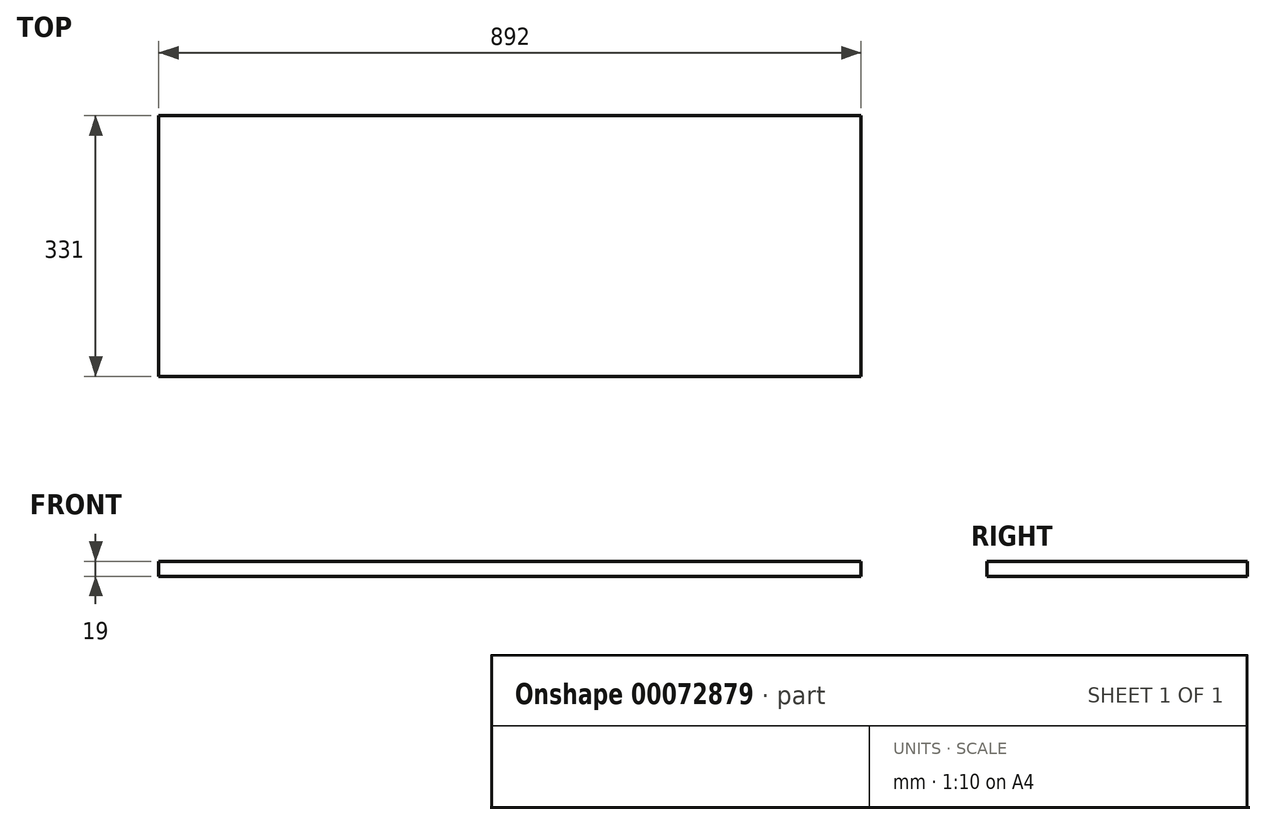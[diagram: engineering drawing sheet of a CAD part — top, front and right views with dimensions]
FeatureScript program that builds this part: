
annotation { "Feature Type Name" : "Feature", "Feature Type Description" : "" }
export const myFeature = defineFeature(function(context is Context, id is Id, definition is map)
    precondition{}
    {
        {
            var Q0;
            Q0=qCreatedBy(makeId("Top.planeOp"),FACE);
            var sketch = newSketch(context, id + "F0", { "sketchPlane" : qUnion([Q0])});
            skLineSegment(sketch, "E0.bottom", {"start": v(0, 0) * mm, "end": v(892, 0) * mm});
            skLineSegment(sketch, "E0.top", {"start": v(0, -331) * mm, "end": v(892, -331) * mm});
            skLineSegment(sketch, "E0.left", {"start": v(0, 0) * mm, "end": v(0, -331) * mm});
            skLineSegment(sketch, "E0.right", {"start": v(892, 0) * mm, "end": v(892, -331) * mm});
            skSolve(sketch);
        }
        {
            var Q0;
            Q0=qSketchRegion(id+"F0",true);
            extrude(context, id + "F1", {"entities" : qUnion([Q0]), "depth" : 19 * mm});
        }
    });
